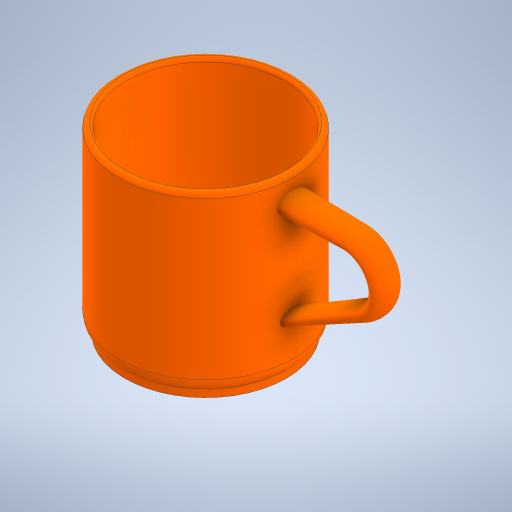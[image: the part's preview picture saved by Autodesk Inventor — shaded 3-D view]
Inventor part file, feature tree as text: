
AUTODESK INVENTOR PART (.ipt)
format: ipt  version: 2024 (Build 280153000, 153)  size: 362,496 bytes
history: native  units: in
note: dims shown in document units (in); Inventor stores cm internally (conversion verified against a paired STEP export)
features: sketch x6, revolve x1, shell x1, plane x1, loft x1, fillet x1, extrude x1, other x1
ambient origin geometry x8: Origin, YZ Plane, XZ Plane, XY Plane, X Axis, Y Axis, Z Axis, Center Point
bodies: Solid1 (feature_tree)
feature tree (13):
  sketch  "Sketch1"  dims[d0=2.7559in d1=1.2795in d2=1.378in]
  revolve  "Revolution1"  [1 undecoded]
  shell  "Shell2"  Thickness=1.378in
  sketch  "Sketch3"  dims[d27=0.4724in d28=0.0in d29=90.0deg]
  plane  "Work Plane2"
  loft  "Loft1"
  fillet  "Fillet1"  Radius=0.1181in
  extrude  "Extrusion1"  TaperAngle=0.0deg  [1 undecoded]
  sketch  "Sketch2"  dims[d3=2.5591in d4=90.0deg d6=0.1181in]
  other  "Work Point2"
  sketch  "Sketch6"  dims[d30=0.0in d31=90.0deg]
  sketch  "Sketch7"  dims[d32=0.0in d33=90.0deg]
  sketch  "Sketch8"  dims[d34=0.0787in d35=2.5591in d36=2.4409in d37=0.1181in d38=0.0in d39=0.0197in d40=0.0344in]
note: 2 required parameter values undecoded (feature->parameter linkage not recoverable at this tier; creation-order binding heuristic only, values carry confidence <= 0.55)